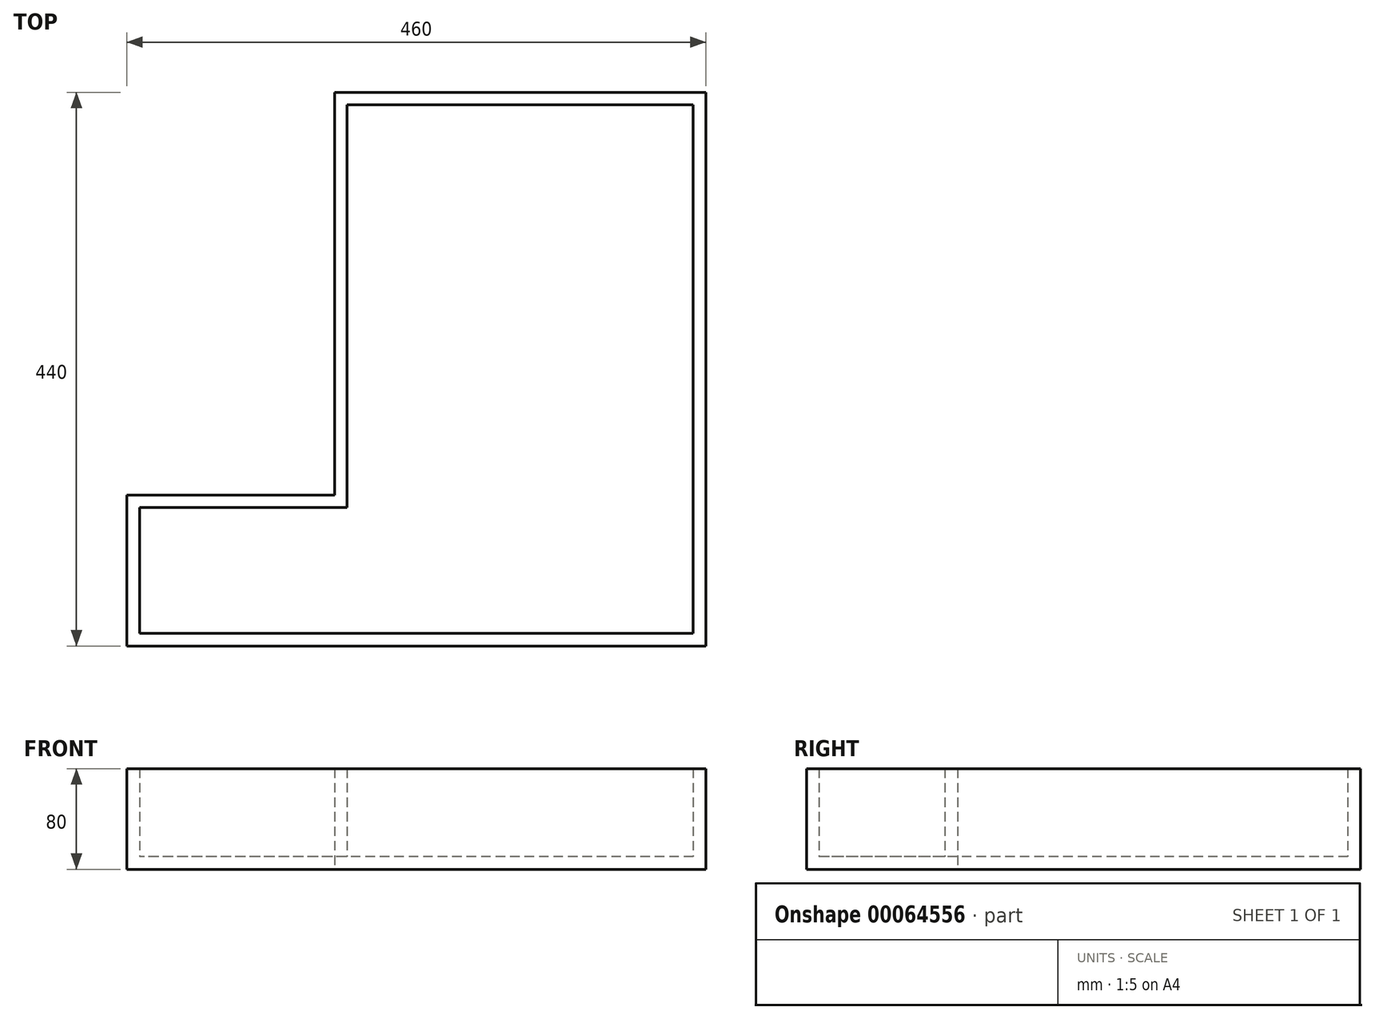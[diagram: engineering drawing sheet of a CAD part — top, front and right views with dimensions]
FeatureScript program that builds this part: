
annotation { "Feature Type Name" : "Feature", "Feature Type Description" : "" }
export const myFeature = defineFeature(function(context is Context, id is Id, definition is map)
    precondition{}
    {
        {
            var Q0;
            Q0=qCreatedBy(makeId("Top.planeOp"),FACE);
            var sketch = newSketch(context, id + "F0", { "sketchPlane" : qUnion([Q0])});
            skLineSegment(sketch, "E0.MirrorCS", {"start": v(412.49, 417.14) * mm, "end": v(117.42, 417.14) * mm});
            skLineSegment(sketch, "E1.MirrorCS", {"start": v(412.49, 417.14) * mm, "end": v(412.49, -22.86) * mm});
            skLineSegment(sketch, "E2.MirrorCS", {"start": v(117.42, 417.14) * mm, "end": v(117.42, 97.14) * mm});
            skLineSegment(sketch, "E3.MirrorCS", {"start": v(412.49, -22.86) * mm, "end": v(-47.51, -22.86) * mm});
            skLineSegment(sketch, "E4.MirrorCS", {"start": v(117.42, 97.14) * mm, "end": v(-47.51, 97.14) * mm});
            skLineSegment(sketch, "E5", {"start": v(-47.51, 97.14) * mm, "end": v(-47.51, -22.86) * mm});
            skSolve(sketch);
        }
        {
            var Q0;
            Q0=makeQuery(id+"F0.imprint","IMPRINT",FACE,{"disambiguationData":[TD([[makeQuery(id+"F0.imprint","IMPRINT",EDGE,{"derivedFrom":sQuery(id+"F0.wireOp",EDGE,"E0.MirrorCS")}),1.0]])]});
            extrude(context, id + "F1", {"entities" : qUnion([Q0]), "depth" : 80 * mm});
        }
        {
            var Q0;
            Q0=makeQuery(id+"F1.opExtrude","CAP_FACE",FACE,{"disambiguationData":[OSD([sQuery(id+"F0.wireOp",EDGE,"E0.MirrorCS"),sQuery(id+"F0.wireOp",EDGE,"E1.MirrorCS"),sQuery(id+"F0.wireOp",EDGE,"E2.MirrorCS"),sQuery(id+"F0.wireOp",EDGE,"E3.MirrorCS"),sQuery(id+"F0.wireOp",EDGE,"E4.MirrorCS"),sQuery(id+"F0.wireOp",EDGE,"E5")])],"isStart":false});
            shell(context, id + "F2", {"entities" : qUnion([Q0]), "thickness" : 10 * mm});
        }
    });
